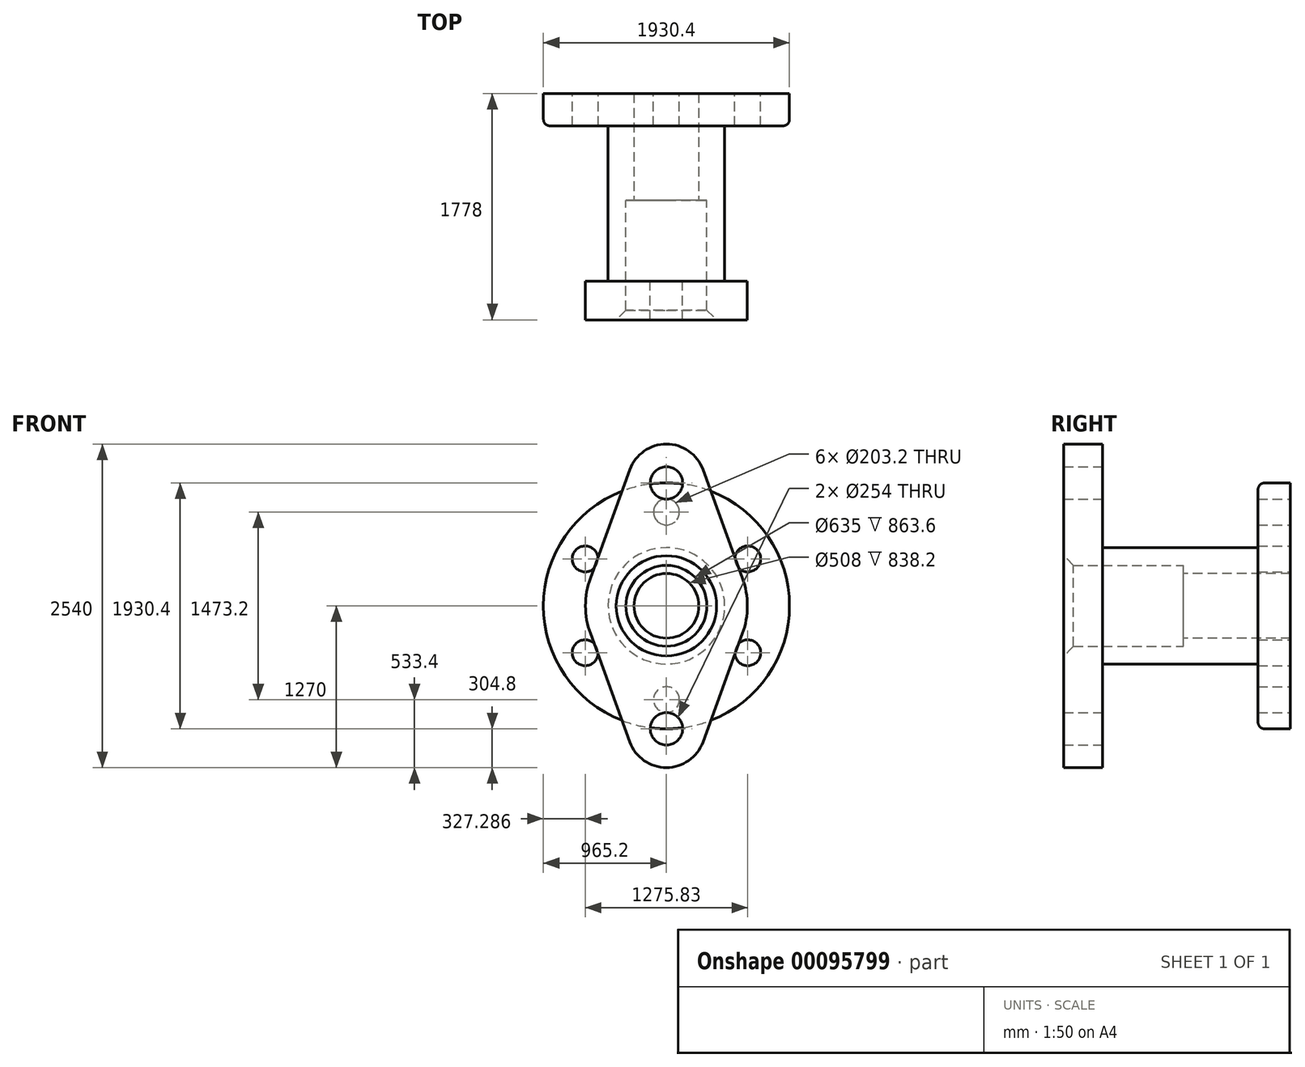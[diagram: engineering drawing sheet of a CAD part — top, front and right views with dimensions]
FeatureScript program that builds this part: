
annotation { "Feature Type Name" : "Feature", "Feature Type Description" : "" }
export const myFeature = defineFeature(function(context is Context, id is Id, definition is map)
    precondition{}
    {
        {
            var Q0;
            Q0=qCreatedBy(makeId("Front.planeOp"),FACE);
            var sketch = newSketch(context, id + "F0", { "sketchPlane" : qUnion([Q0])});
            skCircle(sketch, "E0", {"center": v(0, 0) * mm, "radius": 965.2 * mm});
            skCircle(sketch, "E1", {"center": v(0, 0) * mm, "radius": 736.6 * mm});
            skCircle(sketch, "E2", {"center": v(0, 736.6) * mm, "radius": 101.6 * mm});
            skCircle(sketch, "E3.1.0", {"center": v(-637.91, 368.3) * mm, "radius": 101.6 * mm});
            skCircle(sketch, "E3.2.0", {"center": v(-637.91, -368.3) * mm, "radius": 101.6 * mm});
            skCircle(sketch, "E3.3.0", {"center": v(0, -736.6) * mm, "radius": 101.6 * mm});
            skCircle(sketch, "E3.4.0", {"center": v(637.91, -368.3) * mm, "radius": 101.6 * mm});
            skCircle(sketch, "E3.5.0", {"center": v(637.91, 368.3) * mm, "radius": 101.6 * mm});
            skSolve(sketch);
        }
        {
            var Q0;
            Q0 = qSketchRegion(id + "F0", true);
            var Q1;
            {var subQ1=sQuery(id+"F0.wireOp",EDGE,"E1");var subQ4=sQuery(id+"F0.wireOp",EDGE,"E3.7.0");var subQ22=makeQuery(id+"F0.imprint","INTERSECT",VERTEX,{"disambiguationData":[OD(0.0)],"derivedFrom":[subQ1,subQ4]});Q1=makeQuery(id+"F0.imprint","IMPRINT",FACE,{"disambiguationData":[TD([[makeQuery(id+"F0.imprint","IMPRINT",EDGE,{"disambiguationData":[TD([[subQ22,1.0]])],"derivedFrom":subQ1}),1.0]])]});}
            var Q2;
            {var subQ0=sQuery(id+"F0.wireOp",EDGE,"E3.1.0");var subQ1=sQuery(id+"F0.wireOp",EDGE,"E1");var subQ2=makeQuery(id+"F0.imprint","INTERSECT",VERTEX,{"disambiguationData":[OD(0.0)],"derivedFrom":[subQ1,subQ0]});Q2=makeQuery(id+"F0.imprint","IMPRINT",FACE,{"disambiguationData":[TD([[makeQuery(id+"F0.imprint","IMPRINT",EDGE,{"disambiguationData":[TD([[subQ2,-1.0]])],"derivedFrom":subQ1}),-1.0]])]});}
            var Q3;
            {var subQ0=sQuery(id+"F0.wireOp",EDGE,"E3.1.0");var subQ1=sQuery(id+"F0.wireOp",EDGE,"E1");var subQ2=makeQuery(id+"F0.imprint","INTERSECT",VERTEX,{"disambiguationData":[OD(0.0)],"derivedFrom":[subQ1,subQ0]});Q3=makeQuery(id+"F0.imprint","IMPRINT",FACE,{"disambiguationData":[TD([[makeQuery(id+"F0.imprint","IMPRINT",EDGE,{"disambiguationData":[TD([[subQ2,-1.0]])],"derivedFrom":subQ1}),1.0]])]});}
            var Q4;
            {var subQ0=sQuery(id+"F0.wireOp",EDGE,"E2");var subQ1=sQuery(id+"F0.wireOp",EDGE,"E1");var subQ2=makeQuery(id+"F0.imprint","INTERSECT",VERTEX,{"disambiguationData":[OD(0.0)],"derivedFrom":[subQ1,subQ0]});Q4=makeQuery(id+"F0.imprint","IMPRINT",FACE,{"disambiguationData":[TD([[makeQuery(id+"F0.imprint","IMPRINT",EDGE,{"disambiguationData":[TD([[subQ2,-1.0]])],"derivedFrom":subQ1}),-1.0]])]});}
            var Q5;
            {var subQ0=sQuery(id+"F0.wireOp",EDGE,"E2");var subQ1=sQuery(id+"F0.wireOp",EDGE,"E1");var subQ2=makeQuery(id+"F0.imprint","INTERSECT",VERTEX,{"disambiguationData":[OD(0.0)],"derivedFrom":[subQ1,subQ0]});Q5=makeQuery(id+"F0.imprint","IMPRINT",FACE,{"disambiguationData":[TD([[makeQuery(id+"F0.imprint","IMPRINT",EDGE,{"disambiguationData":[TD([[subQ2,-1.0]])],"derivedFrom":subQ1}),1.0]])]});}
            var Q6;
            {var subQ0=sQuery(id+"F0.wireOp",EDGE,"E3.7.0");var subQ1=sQuery(id+"F0.wireOp",EDGE,"E1");var subQ2=makeQuery(id+"F0.imprint","INTERSECT",VERTEX,{"disambiguationData":[OD(0.0)],"derivedFrom":[subQ1,subQ0]});Q6=makeQuery(id+"F0.imprint","IMPRINT",FACE,{"disambiguationData":[TD([[makeQuery(id+"F0.imprint","IMPRINT",EDGE,{"disambiguationData":[TD([[subQ2,-1.0]])],"derivedFrom":subQ1}),-1.0]])]});}
            var Q7;
            {var subQ0=sQuery(id+"F0.wireOp",EDGE,"E3.7.0");var subQ1=sQuery(id+"F0.wireOp",EDGE,"E1");var subQ2=makeQuery(id+"F0.imprint","INTERSECT",VERTEX,{"disambiguationData":[OD(0.0)],"derivedFrom":[subQ1,subQ0]});Q7=makeQuery(id+"F0.imprint","IMPRINT",FACE,{"disambiguationData":[TD([[makeQuery(id+"F0.imprint","IMPRINT",EDGE,{"disambiguationData":[TD([[subQ2,-1.0]])],"derivedFrom":subQ1}),1.0]])]});}
            var Q8;
            {var subQ0=sQuery(id+"F0.wireOp",EDGE,"E3.6.0");var subQ1=sQuery(id+"F0.wireOp",EDGE,"E1");var subQ2=makeQuery(id+"F0.imprint","INTERSECT",VERTEX,{"disambiguationData":[OD(0.0)],"derivedFrom":[subQ1,subQ0]});Q8=makeQuery(id+"F0.imprint","IMPRINT",FACE,{"disambiguationData":[TD([[makeQuery(id+"F0.imprint","IMPRINT",EDGE,{"disambiguationData":[TD([[subQ2,1.0]])],"derivedFrom":subQ1}),-1.0]])]});}
            var Q9;
            {var subQ0=sQuery(id+"F0.wireOp",EDGE,"E3.6.0");var subQ1=sQuery(id+"F0.wireOp",EDGE,"E1");var subQ2=makeQuery(id+"F0.imprint","INTERSECT",VERTEX,{"disambiguationData":[OD(0.0)],"derivedFrom":[subQ1,subQ0]});Q9=makeQuery(id+"F0.imprint","IMPRINT",FACE,{"disambiguationData":[TD([[makeQuery(id+"F0.imprint","IMPRINT",EDGE,{"disambiguationData":[TD([[subQ2,1.0]])],"derivedFrom":subQ1}),1.0]])]});}
            var Q10;
            {var subQ0=sQuery(id+"F0.wireOp",EDGE,"E3.2.0");var subQ1=sQuery(id+"F0.wireOp",EDGE,"E1");var subQ2=makeQuery(id+"F0.imprint","INTERSECT",VERTEX,{"disambiguationData":[OD(0.0)],"derivedFrom":[subQ1,subQ0]});Q10=makeQuery(id+"F0.imprint","IMPRINT",FACE,{"disambiguationData":[TD([[makeQuery(id+"F0.imprint","IMPRINT",EDGE,{"disambiguationData":[TD([[subQ2,-1.0]])],"derivedFrom":subQ1}),1.0]])]});}
            var Q11;
            {var subQ0=sQuery(id+"F0.wireOp",EDGE,"E3.2.0");var subQ1=sQuery(id+"F0.wireOp",EDGE,"E1");var subQ2=makeQuery(id+"F0.imprint","INTERSECT",VERTEX,{"disambiguationData":[OD(0.0)],"derivedFrom":[subQ1,subQ0]});Q11=makeQuery(id+"F0.imprint","IMPRINT",FACE,{"disambiguationData":[TD([[makeQuery(id+"F0.imprint","IMPRINT",EDGE,{"disambiguationData":[TD([[subQ2,-1.0]])],"derivedFrom":subQ1}),-1.0]])]});}
            var Q12;
            {var subQ0=sQuery(id+"F0.wireOp",EDGE,"E3.3.0");var subQ1=sQuery(id+"F0.wireOp",EDGE,"E1");var subQ2=makeQuery(id+"F0.imprint","INTERSECT",VERTEX,{"disambiguationData":[OD(0.0)],"derivedFrom":[subQ1,subQ0]});Q12=makeQuery(id+"F0.imprint","IMPRINT",FACE,{"disambiguationData":[TD([[makeQuery(id+"F0.imprint","IMPRINT",EDGE,{"disambiguationData":[TD([[subQ2,-1.0]])],"derivedFrom":subQ1}),-1.0]])]});}
            var Q13;
            {var subQ0=sQuery(id+"F0.wireOp",EDGE,"E3.3.0");var subQ1=sQuery(id+"F0.wireOp",EDGE,"E1");var subQ2=makeQuery(id+"F0.imprint","INTERSECT",VERTEX,{"disambiguationData":[OD(0.0)],"derivedFrom":[subQ1,subQ0]});Q13=makeQuery(id+"F0.imprint","IMPRINT",FACE,{"disambiguationData":[TD([[makeQuery(id+"F0.imprint","IMPRINT",EDGE,{"disambiguationData":[TD([[subQ2,-1.0]])],"derivedFrom":subQ1}),1.0]])]});}
            var Q14;
            {var subQ0=sQuery(id+"F0.wireOp",EDGE,"E3.4.0");var subQ1=sQuery(id+"F0.wireOp",EDGE,"E1");var subQ2=makeQuery(id+"F0.imprint","INTERSECT",VERTEX,{"disambiguationData":[OD(0.0)],"derivedFrom":[subQ1,subQ0]});Q14=makeQuery(id+"F0.imprint","IMPRINT",FACE,{"disambiguationData":[TD([[makeQuery(id+"F0.imprint","IMPRINT",EDGE,{"disambiguationData":[TD([[subQ2,-1.0]])],"derivedFrom":subQ1}),-1.0]])]});}
            var Q15;
            {var subQ0=sQuery(id+"F0.wireOp",EDGE,"E3.4.0");var subQ1=sQuery(id+"F0.wireOp",EDGE,"E1");var subQ2=makeQuery(id+"F0.imprint","INTERSECT",VERTEX,{"disambiguationData":[OD(0.0)],"derivedFrom":[subQ1,subQ0]});Q15=makeQuery(id+"F0.imprint","IMPRINT",FACE,{"disambiguationData":[TD([[makeQuery(id+"F0.imprint","IMPRINT",EDGE,{"disambiguationData":[TD([[subQ2,-1.0]])],"derivedFrom":subQ1}),1.0]])]});}
            var Q16;
            {var subQ0=sQuery(id+"F0.wireOp",EDGE,"E3.5.0");var subQ1=sQuery(id+"F0.wireOp",EDGE,"E1");var subQ2=makeQuery(id+"F0.imprint","INTERSECT",VERTEX,{"disambiguationData":[OD(0.0)],"derivedFrom":[subQ1,subQ0]});Q16=makeQuery(id+"F0.imprint","IMPRINT",FACE,{"disambiguationData":[TD([[makeQuery(id+"F0.imprint","IMPRINT",EDGE,{"disambiguationData":[TD([[subQ2,-1.0]])],"derivedFrom":subQ1}),-1.0]])]});}
            var Q17;
            {var subQ0=sQuery(id+"F0.wireOp",EDGE,"E3.5.0");var subQ1=sQuery(id+"F0.wireOp",EDGE,"E1");var subQ2=makeQuery(id+"F0.imprint","INTERSECT",VERTEX,{"disambiguationData":[OD(0.0)],"derivedFrom":[subQ1,subQ0]});Q17=makeQuery(id+"F0.imprint","IMPRINT",FACE,{"disambiguationData":[TD([[makeQuery(id+"F0.imprint","IMPRINT",EDGE,{"disambiguationData":[TD([[subQ2,-1.0]])],"derivedFrom":subQ1}),1.0]])]});}
            var Q18;
            {var subQ0=sQuery(id+"F0.wireOp",EDGE,"E3.5.0");var subQ1=sQuery(id+"F0.wireOp",EDGE,"E1");var subQ2=makeQuery(id+"F0.imprint","INTERSECT",VERTEX,{"disambiguationData":[OD(0.0)],"derivedFrom":[subQ1,subQ0]});Q18=makeQuery(id+"F0.imprint","IMPRINT",FACE,{"disambiguationData":[TD([[makeQuery(id+"F0.imprint","IMPRINT",EDGE,{"disambiguationData":[TD([[subQ2,1.0]])],"derivedFrom":subQ1}),1.0]])]});}
            var Q19;
            {var subQ0=sQuery(id+"F0.wireOp",EDGE,"E3.5.0");var subQ1=sQuery(id+"F0.wireOp",EDGE,"E1");var subQ2=makeQuery(id+"F0.imprint","INTERSECT",VERTEX,{"disambiguationData":[OD(0.0)],"derivedFrom":[subQ1,subQ0]});Q19=makeQuery(id+"F0.imprint","IMPRINT",FACE,{"disambiguationData":[TD([[makeQuery(id+"F0.imprint","IMPRINT",EDGE,{"disambiguationData":[TD([[subQ2,1.0]])],"derivedFrom":subQ1}),-1.0]])]});}
            extrude(context, id + "F1", {"entities" : qUnion([Q0, Q1, Q2, Q3, Q4, Q5, Q6, Q7, Q8, Q9, Q10, Q11, Q12, Q13, Q14, Q15, Q16, Q17, Q18, Q19]), "depth" : 254 * mm});
        }
        {
            var Q0;
            Q0=sQuery(id+"F0.wireOp",VERTEX,"E2.center");
            var Q1;
            Q1=sQuery(id+"F0.wireOp",VERTEX,"E3.1.0.center");
            var Q2;
            Q2=sQuery(id+"F0.wireOp",VERTEX,"E3.2.0.center");
            var Q3;
            Q3=sQuery(id+"F0.wireOp",VERTEX,"E3.3.0.center");
            var Q4;
            Q4=sQuery(id+"F0.wireOp",VERTEX,"E3.4.0.center");
            var Q5;
            Q5=sQuery(id+"F0.wireOp",VERTEX,"E3.5.0.center");
            var Q6;
            Q6=makeQuery(id+"F1.opExtrude","SWEPT_BODY",BODY,{"disambiguationData":[OSD([sQuery(id+"F0.wireOp",EDGE,"E0")])]});
            hole(context, id + "F2", {"style" : HoleStyle.SIMPLE, "endStyle" : HoleEndStyle.THROUGH, "oppositeDirection" : true, "holeDiameter" : 203.2 * mm, "locations" : qUnion([Q0, Q1, Q2, Q3, Q4, Q5]), "scope" : qUnion([Q6]), "isTappedThrough" : true});
        }
        {
            var Q0;
            Q0=makeQuery(id+"F1.opExtrude","CAP_FACE",FACE,{"disambiguationData":[OSD([sQuery(id+"F0.wireOp",EDGE,"E0")])],"isStart":false});
            var sketch = newSketch(context, id + "F3", { "sketchPlane" : qUnion([Q0])});
            skCircle(sketch, "E4", {"center": v(0, 0) * mm, "radius": 457.2 * mm});
            skCircle(sketch, "E5", {"center": v(0, 0) * mm, "radius": 254 * mm});
            skCircle(sketch, "E6", {"center": v(0, 0) * mm, "radius": 317.5 * mm});
            skSolve(sketch);
        }
        {
            var Q0;
            Q0=makeQuery(id+"F3.imprint","IMPRINT",FACE,{"disambiguationData":[TD([[makeQuery(id+"F3.imprint","IMPRINT",EDGE,{"derivedFrom":sQuery(id+"F3.wireOp",EDGE,"E4")}),1.0]])]});
            extrude(context, id + "F4", {"entities" : qUnion([Q0]), "operationType" : NewBodyOperationType.ADD, "depth" : 1219.2 * mm});
        }
        {
            var Q0;
            Q0=makeQuery(id+"F1.opExtrude","CAP_EDGE",EDGE,{"disambiguationData":[OSD([sQuery(id+"F0.wireOp",EDGE,"E0")])],"isStart":false});
            var Q1;
            Q1=makeQuery(id+"F4.opExtrude","CAP_EDGE",EDGE,{"disambiguationData":[OSD([sQuery(id+"F3.wireOp",EDGE,"E4")])],"isStart":true});
            fillet(context, id + "F5", {"entities" : qUnion([Q0, Q1]), "radius" : 50.8 * mm, "tangentPropagation" : true, "allowEdgeOverflow" : false});
        }
        {
            var Q0;
            Q0=makeQuery(id+"F3.imprint","IMPRINT",FACE,{"disambiguationData":[TD([[makeQuery(id+"F3.imprint","IMPRINT",EDGE,{"derivedFrom":sQuery(id+"F3.wireOp",EDGE,"E5")}),1.0]])]});
            extrude(context, id + "F6", {"entities" : qUnion([Q0]), "operationType" : NewBodyOperationType.REMOVE, "endBound" : BoundingType.THROUGH_ALL, "oppositeDirection" : true, "depth" : 2540 * mm});
        }
        {
            var Q0;
            Q0=makeQuery(id+"F3.imprint","IMPRINT",FACE,{"disambiguationData":[TD([[makeQuery(id+"F3.imprint","IMPRINT",EDGE,{"derivedFrom":sQuery(id+"F3.wireOp",EDGE,"E5")}),-1.0]])]});
            extrude(context, id + "F7", {"entities" : qUnion([Q0]), "operationType" : NewBodyOperationType.ADD, "depth" : 584.2 * mm});
        }
        {
            var Q0;
            Q0=makeQuery(id+"F4.opExtrude","CAP_FACE",FACE,{"disambiguationData":[OSD([sQuery(id+"F3.wireOp",EDGE,"E4"),sQuery(id+"F3.wireOp",EDGE,"E6")])],"isStart":false});
            var sketch = newSketch(context, id + "F8", { "sketchPlane" : qUnion([Q0])});
            skLineSegment(sketch, "E7", {"start": v(0, 0) * mm, "end": v(0, 2027.99) * mm});
            skLineSegment(sketch, "E8", {"start": v(0, 0) * mm, "end": v(0, -1830.79) * mm});
            skLineSegment(sketch, "E9", {"start": v(0, 0) * mm, "end": v(-1579.68, 0) * mm});
            skLineSegment(sketch, "E10", {"start": v(0, 0) * mm, "end": v(2023.02, 0) * mm});
            skSolve(sketch);
        }
        {
            var Q0;
            {var subQ0=sQuery(id+"F8.wireOp",EDGE,"E7");var subQ1=makeQuery(id+"F4.opExtrude","CAP_EDGE",EDGE,{"disambiguationData":[OSD([sQuery(id+"F3.wireOp",EDGE,"E4")])],"isStart":false});var subQ2=makeQuery(id+"F8.imprint","INTERSECT",VERTEX,{"derivedFrom":[subQ1,subQ0]});Q0=makeQuery(id+"F8.imprint","IMPRINT",FACE,{"disambiguationData":[TD([[makeQuery(id+"F8.imprint","IMPRINT",EDGE,{"disambiguationData":[TD([[subQ2,1.0]])],"derivedFrom":subQ0}),1.0]])]});}
            var sketch = newSketch(context, id + "F9", { "sketchPlane" : qUnion([Q0])});
            skPoint(sketch, "E11", {"position": v(0, 965.2) * mm});
            skPoint(sketch, "E12", {"position": v(0, -965.2) * mm});
            skCircle(sketch, "E13", {"center": v(0, 965.2) * mm, "radius": 304.8 * mm});
            skCircle(sketch, "E14", {"center": v(0, 965.2) * mm, "radius": 127 * mm});
            skCircle(sketch, "E15", {"center": v(0, -965.2) * mm, "radius": 304.8 * mm});
            skCircle(sketch, "E16", {"center": v(0, -965.2) * mm, "radius": 127 * mm});
            skCircle(sketch, "E17", {"center": v(0, 0) * mm, "radius": 279.4 * mm});
            skCircle(sketch, "E18", {"center": v(0, 0) * mm, "radius": 330.2 * mm});
            skCircle(sketch, "E19", {"center": v(0, 0) * mm, "radius": 635 * mm});
            skLineSegment(sketch, "E20", {"start": v(286.4, 1069.47) * mm, "end": v(597.58, 214.77) * mm});
            skLineSegment(sketch, "E21", {"start": v(596.69, -217.24) * mm, "end": v(248.85, -1172.62) * mm});
            skLineSegment(sketch, "E22", {"start": v(0, 965.2) * mm, "end": v(0, -965.2) * mm});
            skLineSegment(sketch, "E23", {"start": v(-286.4, -1069.47) * mm, "end": v(-675.78, 0) * mm});
            skLineSegment(sketch, "E24", {"start": v(-286.4, 1069.47) * mm, "end": v(-596.69, 217.24) * mm});
            skSolve(sketch);
        }
        {
            var Q0;
            {var subQ13=sQuery(id+"F9.wireOp",EDGE,"ya8A9BkE-coIV-0aEf-c29y-W11fJcQt8qWr");Q0=makeQuery(id+"F9.imprint","IMPRINT",FACE,{"disambiguationData":[TD([[makeQuery(id+"F9.imprint","IMPRINT",EDGE,{"derivedFrom":subQ13}),-1.0]])]});}
            var Q1;
            {var subQ1=sQuery(id+"F8.wireOp",EDGE,"E7");var subQ2=makeQuery(id+"F4.opExtrude","CAP_EDGE",EDGE,{"disambiguationData":[OSD([sQuery(id+"F3.wireOp",EDGE,"E4")])],"isStart":false});var subQ3=makeQuery(id+"F8.imprint","INTERSECT",VERTEX,{"derivedFrom":[subQ2,subQ1]});var subQ11=makeQuery(id+"F8.imprint","IMPRINT",EDGE,{"disambiguationData":[TD([[subQ3,-1.0]])],"derivedFrom":subQ2});Q1=makeQuery(id+"F9.imprint","IMPRINT",FACE,{"disambiguationData":[TD([[makeQuery(id+"F9.imprint","IMPRINT",EDGE,{"derivedFrom":subQ11}),1.0]])]});}
            var Q2;
            Q2=makeQuery(id+"F9.imprint","IMPRINT",FACE,{"disambiguationData":[TD([[makeQuery(id+"F9.imprint","IMPRINT",EDGE,{"derivedFrom":sQuery(id+"F9.wireOp",EDGE,"E16")}),-1.0]])]});
            var Q3;
            {var subQ0=sQuery(id+"F9.wireOp",EDGE,"qZcp2iFD-yTbO-aO5D-vJsB-K42KSH7r9xvT");var subQ1=makeQuery(id+"F9.imprint","INTERSECT",VERTEX,{"derivedFrom":[subQ0,sQuery(id+"F9.wireOp",EDGE,"eW8BNkMa-DnNI-QZdu-Olqy-l7O4oWZxZ6XR")]});Q3=makeQuery(id+"F9.imprint","IMPRINT",FACE,{"disambiguationData":[TD([[makeQuery(id+"F9.imprint","IMPRINT",EDGE,{"disambiguationData":[TD([[subQ1,-1.0]])],"derivedFrom":subQ0}),1.0]])]});}
            var Q4;
            {var subQ0=sQuery(id+"F9.wireOp",EDGE,"h6m9uejH-BYQN-DJct-PYJt-bV2pgaKJldlE");var subQ1=makeQuery(id+"F9.imprint","INTERSECT",VERTEX,{"derivedFrom":[subQ0,sQuery(id+"F9.wireOp",EDGE,"ya8A9BkE-coIV-0aEf-c29y-W11fJcQt8qWr")]});Q4=makeQuery(id+"F9.imprint","IMPRINT",FACE,{"disambiguationData":[TD([[makeQuery(id+"F9.imprint","IMPRINT",EDGE,{"disambiguationData":[TD([[subQ1,-1.0]])],"derivedFrom":subQ0}),1.0]])]});}
            var Q5;
            Q5=makeQuery(id+"F9.imprint","IMPRINT",FACE,{"disambiguationData":[TD([[makeQuery(id+"F9.imprint","IMPRINT",EDGE,{"derivedFrom":sQuery(id+"F9.wireOp",EDGE,"E14")}),-1.0]])]});
            var Q6;
            {var subQ0=sQuery(id+"F9.wireOp",EDGE,"E24");Q6=makeQuery(id+"F9.imprint","IMPRINT",FACE,{"disambiguationData":[TD([[makeQuery(id+"F9.imprint","IMPRINT",EDGE,{"derivedFrom":subQ0}),1.0]])]});}
            var Q7;
            {var subQ0=sQuery(id+"F9.wireOp",EDGE,"E19");var subQ4=makeQuery(id+"F9.imprint","INTERSECT",VERTEX,{"derivedFrom":[subQ0,sQuery(id+"F9.wireOp",EDGE,"E24")]});Q7=makeQuery(id+"F9.imprint","IMPRINT",FACE,{"disambiguationData":[TD([[makeQuery(id+"F9.imprint","IMPRINT",EDGE,{"disambiguationData":[TD([[subQ4,1.0]])],"derivedFrom":subQ0}),1.0]])]});}
            var Q8;
            {var subQ0=sQuery(id+"F9.wireOp",EDGE,"E20");var subQ1=sQuery(id+"F9.wireOp",EDGE,"E13");var subQ2=makeQuery(id+"F9.imprint","INTERSECT",VERTEX,{"derivedFrom":[subQ1,subQ0]});Q8=makeQuery(id+"F9.imprint","IMPRINT",FACE,{"disambiguationData":[TD([[makeQuery(id+"F9.imprint","IMPRINT",EDGE,{"disambiguationData":[TD([[subQ2,1.0]])],"derivedFrom":subQ1}),-1.0]])]});}
            var Q9;
            {var subQ3=sQuery(id+"F9.wireOp",EDGE,"E22");var subQ6=sQuery(id+"F9.wireOp",EDGE,"E18");var subQ7=makeQuery(id+"F9.imprint","INTERSECT",VERTEX,{"disambiguationData":[OD(0.0)],"derivedFrom":[subQ6,subQ3]});Q9=makeQuery(id+"F9.imprint","IMPRINT",FACE,{"disambiguationData":[TD([[makeQuery(id+"F9.imprint","IMPRINT",EDGE,{"disambiguationData":[TD([[subQ7,1.0]])],"derivedFrom":subQ6}),-1.0]])]});}
            var Q10;
            {var subQ0=sQuery(id+"F9.wireOp",EDGE,"E21");var subQ1=sQuery(id+"F9.wireOp",EDGE,"E15");var subQ2=makeQuery(id+"F9.imprint","INTERSECT",VERTEX,{"derivedFrom":[subQ1,subQ0]});Q10=makeQuery(id+"F9.imprint","IMPRINT",FACE,{"disambiguationData":[TD([[makeQuery(id+"F9.imprint","IMPRINT",EDGE,{"disambiguationData":[TD([[subQ2,-1.0]])],"derivedFrom":subQ1}),-1.0]])]});}
            var Q11;
            {var subQ0=sQuery(id+"F9.wireOp",EDGE,"E23");var subQ1=sQuery(id+"F9.wireOp",EDGE,"E15");var subQ2=makeQuery(id+"F9.imprint","INTERSECT",VERTEX,{"derivedFrom":[subQ1,subQ0]});Q11=makeQuery(id+"F9.imprint","IMPRINT",FACE,{"disambiguationData":[TD([[makeQuery(id+"F9.imprint","IMPRINT",EDGE,{"disambiguationData":[TD([[subQ2,1.0]])],"derivedFrom":subQ1}),-1.0]])]});}
            extrude(context, id + "F10", {"entities" : qUnion([Q0, Q1, Q2, Q3, Q4, Q5, Q6, Q7, Q8, Q9, Q10, Q11]), "operationType" : NewBodyOperationType.ADD, "depth" : 304.8 * mm});
        }
        {
            var Q0;
            {var subQ0=sQuery(id+"F8.wireOp",EDGE,"E8");var subQ1=makeQuery(id+"F4.opExtrude","CAP_EDGE",EDGE,{"disambiguationData":[OSD([sQuery(id+"F3.wireOp",EDGE,"E4")])],"isStart":false});var subQ2=makeQuery(id+"F8.imprint","INTERSECT",VERTEX,{"derivedFrom":[subQ1,subQ0]});Q0=makeQuery(id+"F8.imprint","IMPRINT",FACE,{"disambiguationData":[TD([[makeQuery(id+"F8.imprint","IMPRINT",EDGE,{"disambiguationData":[TD([[subQ2,1.0]])],"derivedFrom":subQ0}),-1.0]])]});}
            var Q1;
            {var subQ0=sQuery(id+"F8.wireOp",EDGE,"E7");var subQ1=makeQuery(id+"F4.opExtrude","CAP_EDGE",EDGE,{"disambiguationData":[OSD([sQuery(id+"F3.wireOp",EDGE,"E4")])],"isStart":false});var subQ2=makeQuery(id+"F8.imprint","INTERSECT",VERTEX,{"derivedFrom":[subQ1,subQ0]});Q1=makeQuery(id+"F8.imprint","IMPRINT",FACE,{"disambiguationData":[TD([[makeQuery(id+"F8.imprint","IMPRINT",EDGE,{"disambiguationData":[TD([[subQ2,1.0]])],"derivedFrom":subQ0}),1.0]])]});}
            var Q2;
            {var subQ0=sQuery(id+"F8.wireOp",EDGE,"E7");var subQ1=makeQuery(id+"F4.opExtrude","CAP_EDGE",EDGE,{"disambiguationData":[OSD([sQuery(id+"F3.wireOp",EDGE,"E4")])],"isStart":false});var subQ2=makeQuery(id+"F8.imprint","INTERSECT",VERTEX,{"derivedFrom":[subQ1,subQ0]});Q2=makeQuery(id+"F8.imprint","IMPRINT",FACE,{"disambiguationData":[TD([[makeQuery(id+"F8.imprint","IMPRINT",EDGE,{"disambiguationData":[TD([[subQ2,1.0]])],"derivedFrom":subQ0}),-1.0]])]});}
            var Q3;
            {var subQ0=sQuery(id+"F8.wireOp",EDGE,"E8");var subQ1=makeQuery(id+"F4.opExtrude","CAP_EDGE",EDGE,{"disambiguationData":[OSD([sQuery(id+"F3.wireOp",EDGE,"E4")])],"isStart":false});var subQ2=makeQuery(id+"F8.imprint","INTERSECT",VERTEX,{"derivedFrom":[subQ1,subQ0]});Q3=makeQuery(id+"F8.imprint","IMPRINT",FACE,{"disambiguationData":[TD([[makeQuery(id+"F8.imprint","IMPRINT",EDGE,{"disambiguationData":[TD([[subQ2,1.0]])],"derivedFrom":subQ0}),1.0]])]});}
            extrude(context, id + "F11", {"entities" : qUnion([Q0, Q1, Q2, Q3]), "operationType" : NewBodyOperationType.ADD, "depth" : 304.8 * mm});
        }
        {
            var Q0;
            Q0=makeQuery(id+"F11.opExtrude","CAP_EDGE",EDGE,{"disambiguationData":[OSD([sQuery(id+"F3.wireOp",EDGE,"E6")])],"isStart":false});
            chamfer(context, id + "F12", {"entities" : qUnion([Q0]), "chamferType" : ChamferType.OFFSET_ANGLE, "width" : 76.2 * mm, "oppositeDirection" : false, "angle" : 45 * degree, "tangentPropagation" : true});
        }
    });
